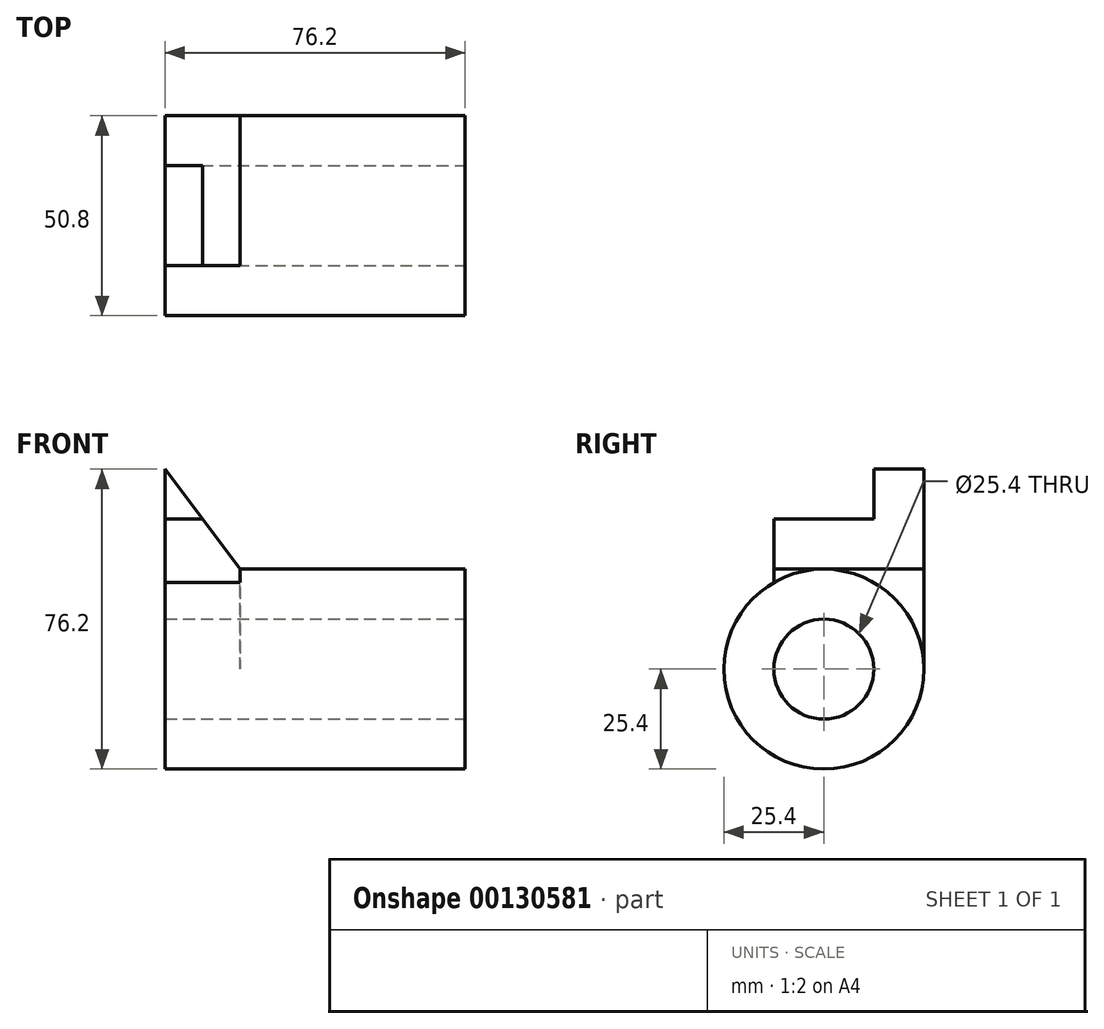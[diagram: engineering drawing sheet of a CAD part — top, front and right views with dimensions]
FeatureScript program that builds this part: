
annotation { "Feature Type Name" : "Feature", "Feature Type Description" : "" }
export const myFeature = defineFeature(function(context is Context, id is Id, definition is map)
    precondition{}
    {
        {
            var Q0;
            Q0=qCreatedBy(makeId("Front.planeOp"),FACE);
            var sketch = newSketch(context, id + "F0", { "sketchPlane" : qUnion([Q0])});
            skLineSegment(sketch, "E0", {"start": v(0, 0) * mm, "end": v(0, 76.2) * mm});
            skLineSegment(sketch, "E1", {"start": v(0, 76.2) * mm, "end": v(9.52, 63.5) * mm});
            skLineSegment(sketch, "E2", {"start": v(9.53, 63.5) * mm, "end": v(0, 63.5) * mm});
            skLineSegment(sketch, "E3", {"start": v(21.9, 47) * mm, "end": v(9.52, 63.5) * mm});
            skLineSegment(sketch, "E4", {"start": v(50.8, 50.8) * mm, "end": v(50.8, 15.88) * mm});
            skLineSegment(sketch, "E5", {"start": v(50.8, 15.88) * mm, "end": v(63.5, 15.88) * mm});
            skLineSegment(sketch, "E6", {"start": v(63.5, 15.88) * mm, "end": v(63.5, 34.93) * mm});
            skLineSegment(sketch, "E7", {"start": v(63.5, 34.93) * mm, "end": v(76.2, 34.93) * mm});
            skLineSegment(sketch, "E8", {"start": v(76.2, 34.93) * mm, "end": v(76.2, 0) * mm});
            skLineSegment(sketch, "E9", {"start": v(76.2, 0) * mm, "end": v(0, 0) * mm});
            skLineSegment(sketch, "E10", {"start": v(50.8, 50.8) * mm, "end": v(19.05, 50.8) * mm});
            skLineSegment(sketch, "E11", {"start": v(21.9, 47) * mm, "end": v(0, 47) * mm});
            skSolve(sketch);
        }
        {
            var Q0;
            Q0=makeQuery(id+"F0.imprint","IMPRINT",FACE,{"disambiguationData":[TD([[makeQuery(id+"F0.imprint","IMPRINT",EDGE,{"derivedFrom":sQuery(id+"F0.wireOp",EDGE,"E4")}),-1.0]])]});
            extrude(context, id + "F1", {"entities" : qUnion([Q0]), "depth" : 50.8 * mm});
        }
        {
            var Q0;
            {var subQ1=sQuery(id+"F0.wireOp",EDGE,"E2");Q0=makeQuery(id+"F0.imprint","IMPRINT",FACE,{"disambiguationData":[TD([[makeQuery(id+"F0.imprint","IMPRINT",EDGE,{"derivedFrom":subQ1}),1.0]])]});}
            extrude(context, id + "F2", {"entities" : qUnion([Q0]), "operationType" : NewBodyOperationType.ADD, "depth" : 38.1 * mm});
        }
        {
            var Q0;
            {var subQ0=sQuery(id+"F0.wireOp",EDGE,"E1");Q0=makeQuery(id+"F0.imprint","IMPRINT",FACE,{"disambiguationData":[TD([[makeQuery(id+"F0.imprint","IMPRINT",EDGE,{"derivedFrom":subQ0}),-1.0]])]});}
            extrude(context, id + "F3", {"entities" : qUnion([Q0]), "operationType" : NewBodyOperationType.ADD, "depth" : 12.7 * mm});
        }
        {
            var Q0;
            Q0=makeQuery(id+"F1.opExtrude","SWEPT_FACE",FACE,{"disambiguationData":[OSD([sQuery(id+"F0.wireOp",EDGE,"E8")])]});
            var sketch = newSketch(context, id + "F4", { "sketchPlane" : qUnion([Q0])});
            skLineSegment(sketch, "E12", {"start": v(-25.4, 62.7) * mm, "end": v(-25.4, 0) * mm, "construction": true});
            skPoint(sketch, "E12.startSnap0", {"position": v(-25.4, 34.93) * mm});
            skLineSegment(sketch, "E13", {"start": v(-50.8, 25.4) * mm, "end": v(0, 25.4) * mm, "construction": true});
            skCircle(sketch, "E14", {"center": v(-25.4, 25.4) * mm, "radius": 12.7 * mm});
            skCircle(sketch, "E15", {"center": v(-25.4, 25.4) * mm, "radius": 25.4 * mm});
            skSolve(sketch);
        }
        {
            var Q0;
            {var subQ0=sQuery(id+"F4.wireOp",EDGE,"E14");var subQ1=makeQuery(id+"F1.opExtrude","SWEPT_EDGE",EDGE,{"disambiguationData":[OSD([sQuery(id+"F0.wireOp",EDGE,"E7"),sQuery(id+"F0.wireOp",EDGE,"E8")])]});var subQ2=makeQuery(id+"F4.imprint","INTERSECT",VERTEX,{"disambiguationData":[OD(0.0)],"derivedFrom":[subQ1,subQ0]});Q0=makeQuery(id+"F4.imprint","IMPRINT",FACE,{"disambiguationData":[TD([[makeQuery(id+"F4.imprint","IMPRINT",EDGE,{"disambiguationData":[TD([[subQ2,1.0]])],"derivedFrom":subQ0}),1.0]])]});}
            var Q1;
            {var subQ0=sQuery(id+"F4.wireOp",EDGE,"E14");var subQ1=makeQuery(id+"F1.opExtrude","SWEPT_EDGE",EDGE,{"disambiguationData":[OSD([sQuery(id+"F0.wireOp",EDGE,"E7"),sQuery(id+"F0.wireOp",EDGE,"E8")])]});var subQ2=makeQuery(id+"F4.imprint","INTERSECT",VERTEX,{"disambiguationData":[OD(0.0)],"derivedFrom":[subQ1,subQ0]});Q1=makeQuery(id+"F4.imprint","IMPRINT",FACE,{"disambiguationData":[TD([[makeQuery(id+"F4.imprint","IMPRINT",EDGE,{"disambiguationData":[TD([[subQ2,-1.0]])],"derivedFrom":subQ0}),1.0]])]});}
            extrude(context, id + "F5", {"entities" : qUnion([Q0, Q1]), "operationType" : NewBodyOperationType.REMOVE, "endBound" : BoundingType.THROUGH_ALL, "oppositeDirection" : true, "depth" : 25.4 * mm});
        }
        {
            var Q0;
            {var subQ0=sQuery(id+"F4.wireOp",EDGE,"E15");var subQ1=sQuery(id+"F0.wireOp",EDGE,"E8");var subQ9=makeQuery(id+"F4.imprint","INTERSECT",VERTEX,{"derivedFrom":[makeQuery(id+"F1.opExtrude","CAP_EDGE",EDGE,{"disambiguationData":[OSD([subQ1])],"isStart":true}),subQ0]});Q0=makeQuery(id+"F4.imprint","IMPRINT",FACE,{"disambiguationData":[TD([[makeQuery(id+"F4.imprint","IMPRINT",EDGE,{"disambiguationData":[TD([[subQ9,-1.0]])],"derivedFrom":subQ0}),1.0]])]});}
            var Q1;
            {var subQ0=sQuery(id+"F4.wireOp",EDGE,"E14");var subQ1=makeQuery(id+"F1.opExtrude","SWEPT_EDGE",EDGE,{"disambiguationData":[OSD([sQuery(id+"F0.wireOp",EDGE,"E7"),sQuery(id+"F0.wireOp",EDGE,"E8")])]});var subQ2=makeQuery(id+"F4.imprint","INTERSECT",VERTEX,{"disambiguationData":[OD(0.0)],"derivedFrom":[subQ1,subQ0]});Q1=makeQuery(id+"F4.imprint","IMPRINT",FACE,{"disambiguationData":[TD([[makeQuery(id+"F4.imprint","IMPRINT",EDGE,{"disambiguationData":[TD([[subQ2,-1.0]])],"derivedFrom":subQ0}),-1.0]])]});}
            extrude(context, id + "F6", {"entities" : qUnion([Q0, Q1]), "operationType" : NewBodyOperationType.ADD, "oppositeDirection" : true, "depth" : 76.2 * mm});
        }
        {
            var Q0;
            {var subQ0=sQuery(id+"F4.wireOp",EDGE,"E15");var subQ1=sQuery(id+"F0.wireOp",EDGE,"E8");var subQ2=makeQuery(id+"F1.opExtrude","CAP_EDGE",EDGE,{"disambiguationData":[OSD([subQ1])],"isStart":false});var subQ3=makeQuery(id+"F4.imprint","INTERSECT",VERTEX,{"derivedFrom":[subQ2,subQ0]});Q0=makeQuery(id+"F4.imprint","IMPRINT",FACE,{"disambiguationData":[TD([[makeQuery(id+"F4.imprint","IMPRINT",EDGE,{"disambiguationData":[TD([[subQ3,-1.0]])],"derivedFrom":subQ0}),-1.0]])]});}
            var Q1;
            {var subQ0=sQuery(id+"F4.wireOp",EDGE,"E15");var subQ1=sQuery(id+"F0.wireOp",EDGE,"E8");var subQ2=makeQuery(id+"F1.opExtrude","CAP_EDGE",EDGE,{"disambiguationData":[OSD([subQ1])],"isStart":true});var subQ3=makeQuery(id+"F4.imprint","INTERSECT",VERTEX,{"derivedFrom":[subQ2,subQ0]});Q1=makeQuery(id+"F4.imprint","IMPRINT",FACE,{"disambiguationData":[TD([[makeQuery(id+"F4.imprint","IMPRINT",EDGE,{"disambiguationData":[TD([[subQ3,1.0]])],"derivedFrom":subQ0}),-1.0]])]});}
            var Q2;
            {var subQ0=sQuery(id+"F4.wireOp",EDGE,"E15");var subQ1=sQuery(id+"F0.wireOp",EDGE,"E8");var subQ4=makeQuery(id+"F1.opExtrude","CAP_EDGE",EDGE,{"disambiguationData":[OSD([subQ1])],"isStart":false});var subQ5=makeQuery(id+"F4.imprint","INTERSECT",VERTEX,{"derivedFrom":[subQ4,subQ0]});Q2=makeQuery(id+"F4.imprint","IMPRINT",FACE,{"disambiguationData":[TD([[makeQuery(id+"F4.imprint","IMPRINT",EDGE,{"disambiguationData":[TD([[subQ5,1.0]])],"derivedFrom":subQ0}),-1.0]])]});}
            var Q3;
            {var subQ0=sQuery(id+"F4.wireOp",EDGE,"E15");var subQ1=sQuery(id+"F0.wireOp",EDGE,"E8");var subQ4=makeQuery(id+"F1.opExtrude","CAP_EDGE",EDGE,{"disambiguationData":[OSD([subQ1])],"isStart":true});var subQ5=makeQuery(id+"F4.imprint","INTERSECT",VERTEX,{"derivedFrom":[subQ4,subQ0]});Q3=makeQuery(id+"F4.imprint","IMPRINT",FACE,{"disambiguationData":[TD([[makeQuery(id+"F4.imprint","IMPRINT",EDGE,{"disambiguationData":[TD([[subQ5,-1.0]])],"derivedFrom":subQ0}),-1.0]])]});}
            extrude(context, id + "F7", {"entities" : qUnion([Q0, Q1, Q2, Q3]), "operationType" : NewBodyOperationType.REMOVE, "endBound" : BoundingType.THROUGH_ALL, "oppositeDirection" : true, "depth" : 25.4 * mm});
        }
        {
            var Q0;
            {var subQ0=sQuery(id+"F0.wireOp",EDGE,"E10");var subQ1=sQuery(id+"F0.wireOp",EDGE,"E11");var subQ2=sQuery(id+"F0.wireOp",EDGE,"E3");var subQ3=sQuery(id+"F0.wireOp",EDGE,"E2");var subQ4=sQuery(id+"F0.wireOp",EDGE,"E0");var subQ5=sQuery(id+"F0.wireOp",EDGE,"E4");var subQ6=makeQuery(id+"F1.opExtrude","SWEPT_FACE",FACE,{"disambiguationData":[OSD([subQ5])]});Q0=makeQuery(id+"F6.boolean.opBoolean","SPLIT",FACE,{"disambiguationData":[TD([makeQuery(id+"F1.opExtrude","CAP_FACE",FACE,{"disambiguationData":[OSD([subQ4,subQ2,subQ5,sQuery(id+"F0.wireOp",EDGE,"E5"),sQuery(id+"F0.wireOp",EDGE,"E6"),sQuery(id+"F0.wireOp",EDGE,"E7"),sQuery(id+"F0.wireOp",EDGE,"E8"),sQuery(id+"F0.wireOp",EDGE,"E9"),subQ0,subQ1])],"isStart":true}),subQ6,makeQuery(id+"F1.opExtrude","SWEPT_FACE",FACE,{"disambiguationData":[OSD([subQ0])]}),makeQuery(id+"F2.opExtrude","CAP_FACE",FACE,{"disambiguationData":[OSD([subQ4,subQ3,subQ2,subQ1])],"isStart":true}),makeQuery(id+"F3.opExtrude","CAP_FACE",FACE,{"disambiguationData":[OSD([subQ4,sQuery(id+"F0.wireOp",EDGE,"E1"),subQ3])],"isStart":true}),makeQuery(id+"F6.opExtrude","SWEPT_FACE",FACE,{"disambiguationData":[OSD([sQuery(id+"F4.wireOp",EDGE,"E15")])]})])],"derivedFrom":subQ6});}
            var Q1;
            {var subQ0=sQuery(id+"F0.wireOp",EDGE,"E10");var subQ1=sQuery(id+"F0.wireOp",EDGE,"E4");var subQ2=makeQuery(id+"F1.opExtrude","SWEPT_FACE",FACE,{"disambiguationData":[OSD([subQ1])]});Q1=makeQuery(id+"F6.boolean.opBoolean","SPLIT",FACE,{"disambiguationData":[TD([makeQuery(id+"F1.opExtrude","CAP_FACE",FACE,{"disambiguationData":[OSD([sQuery(id+"F0.wireOp",EDGE,"E0"),sQuery(id+"F0.wireOp",EDGE,"E3"),subQ1,sQuery(id+"F0.wireOp",EDGE,"E5"),sQuery(id+"F0.wireOp",EDGE,"E6"),sQuery(id+"F0.wireOp",EDGE,"E7"),sQuery(id+"F0.wireOp",EDGE,"E8"),sQuery(id+"F0.wireOp",EDGE,"E9"),subQ0,sQuery(id+"F0.wireOp",EDGE,"E11")])],"isStart":false}),subQ2,makeQuery(id+"F1.opExtrude","SWEPT_FACE",FACE,{"disambiguationData":[OSD([subQ0])]}),makeQuery(id+"F6.opExtrude","SWEPT_FACE",FACE,{"disambiguationData":[OSD([sQuery(id+"F4.wireOp",EDGE,"E15")])]})])],"derivedFrom":subQ2});}
            extrude(context, id + "F8", {"entities" : qUnion([Q0, Q1]), "operationType" : NewBodyOperationType.REMOVE, "endBound" : BoundingType.THROUGH_ALL, "oppositeDirection" : true, "depth" : 70.73 * mm});
        }
        {
            var Q0;
            Q0=qCreatedBy(makeId("Right.planeOp"),FACE);
            var sketch = newSketch(context, id + "F9", { "sketchPlane" : qUnion([Q0])});
            skLineSegment(sketch, "E16", {"start": v(0, 50.8) * mm, "end": v(0, 25.4) * mm});
            skLineSegment(sketch, "E17", {"start": v(-38.1, 50.8) * mm, "end": v(-38.1, 47.4) * mm});
            skLineSegment(sketch, "E18", {"start": v(0, 50.8) * mm, "end": v(-38.1, 50.8) * mm});
            skLineSegment(sketch, "E19", {"start": v(-25.4, 50.8) * mm, "end": v(-25.4, 0) * mm, "construction": true});
            skArc(sketch, "E20", {"start": v(0, 25.4) * mm, "mid": v(-7.44, 43.36) * mm, "end": v(-25.4, 50.8) * mm});
            skArc(sketch, "E21", {"start": v(-25.4, 50.8) * mm, "mid": v(-31.97, 49.93) * mm, "end": v(-38.1, 47.4) * mm});
            skSolve(sketch);
        }
        {
            var Q0;
            {var subQ0=sQuery(id+"F9.wireOp",EDGE,"E16");Q0=makeQuery(id+"F9.imprint","IMPRINT",FACE,{"disambiguationData":[TD([[makeQuery(id+"F9.imprint","IMPRINT",EDGE,{"derivedFrom":subQ0}),-1.0]])]});}
            var Q1;
            {var subQ0=sQuery(id+"F9.wireOp",EDGE,"E17");Q1=makeQuery(id+"F9.imprint","IMPRINT",FACE,{"disambiguationData":[TD([[makeQuery(id+"F9.imprint","IMPRINT",EDGE,{"derivedFrom":subQ0}),1.0]])]});}
            extrude(context, id + "F10", {"entities" : qUnion([Q0, Q1]), "operationType" : NewBodyOperationType.ADD, "depth" : 19.05 * mm});
        }
    });
